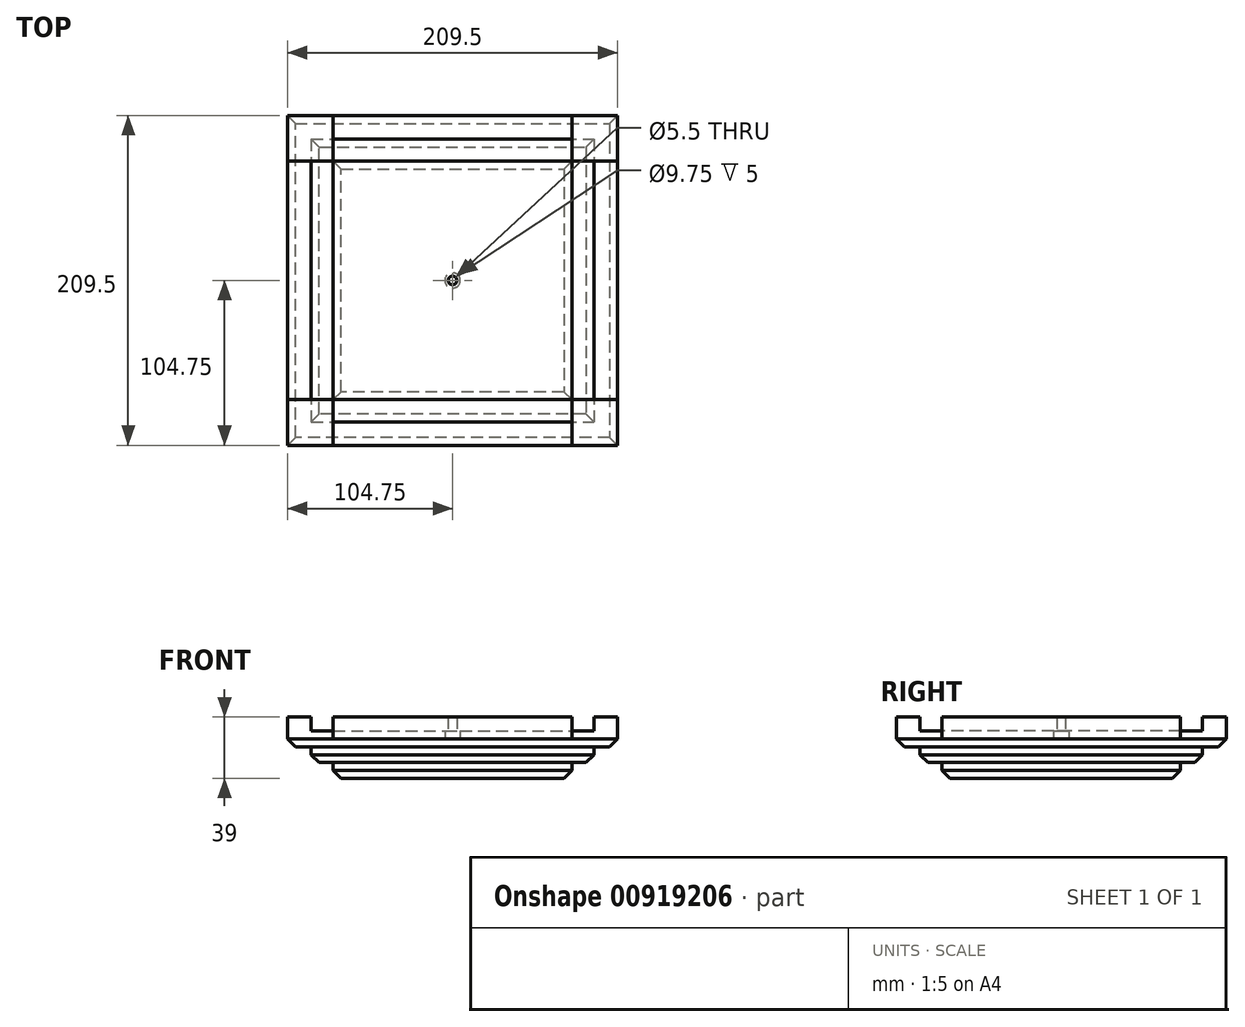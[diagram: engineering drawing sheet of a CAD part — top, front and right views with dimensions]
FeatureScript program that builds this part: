
annotation { "Feature Type Name" : "Feature", "Feature Type Description" : "" }
export const myFeature = defineFeature(function(context is Context, id is Id, definition is map)
    precondition{}
    {
        {
            var Q0;
            Q0=qCreatedBy(makeId("Top.planeOp"),FACE);
            var sketch = newSketch(context, id + "F0", { "sketchPlane" : qUnion([Q0])});
            skLineSegment(sketch, "E0.bottom", {"start": v(-104.75, 104.75) * mm, "end": v(104.75, 104.75) * mm});
            skLineSegment(sketch, "E0.top", {"start": v(-104.75, -104.75) * mm, "end": v(104.75, -104.75) * mm});
            skLineSegment(sketch, "E0.left", {"start": v(-104.75, 104.75) * mm, "end": v(-104.75, -104.75) * mm});
            skLineSegment(sketch, "E0.right", {"start": v(104.75, 104.75) * mm, "end": v(104.75, -104.75) * mm});
            skLineSegment(sketch, "E1.bottom", {"start": v(-75.75, 75.75) * mm, "end": v(75.75, 75.75) * mm});
            skLineSegment(sketch, "E1.top", {"start": v(-75.75, -75.75) * mm, "end": v(75.75, -75.75) * mm});
            skLineSegment(sketch, "E1.left", {"start": v(-75.75, 75.75) * mm, "end": v(-75.75, -75.75) * mm});
            skLineSegment(sketch, "E1.right", {"start": v(75.75, 75.75) * mm, "end": v(75.75, -75.75) * mm});
            skLineSegment(sketch, "E2.0", {"start": v(-89.75, 89.75) * mm, "end": v(-89.75, -89.75) * mm});
            skLineSegment(sketch, "E2.1", {"start": v(-89.75, 89.75) * mm, "end": v(89.75, 89.75) * mm});
            skLineSegment(sketch, "E2.2", {"start": v(89.75, 89.75) * mm, "end": v(89.75, -89.75) * mm});
            skLineSegment(sketch, "E2.3", {"start": v(-89.75, -89.75) * mm, "end": v(89.75, -89.75) * mm});
            skLineSegment(sketch, "E3.bottom", {"start": v(-75.75, 75.75) * mm, "end": v(-104.75, 75.75) * mm});
            skLineSegment(sketch, "E3.top", {"start": v(-75.75, 104.75) * mm, "end": v(-104.75, 104.75) * mm});
            skLineSegment(sketch, "E3.left", {"start": v(-75.75, 75.75) * mm, "end": v(-75.75, 104.75) * mm});
            skLineSegment(sketch, "E3.right", {"start": v(-104.75, 75.75) * mm, "end": v(-104.75, 104.75) * mm});
            skLineSegment(sketch, "E4.bottom", {"start": v(75.75, 75.75) * mm, "end": v(104.75, 75.75) * mm});
            skLineSegment(sketch, "E4.top", {"start": v(75.75, 104.75) * mm, "end": v(104.75, 104.75) * mm});
            skLineSegment(sketch, "E4.left", {"start": v(75.75, 75.75) * mm, "end": v(75.75, 104.75) * mm});
            skLineSegment(sketch, "E4.right", {"start": v(104.75, 75.75) * mm, "end": v(104.75, 104.75) * mm});
            skLineSegment(sketch, "E5.bottom", {"start": v(75.75, -75.75) * mm, "end": v(104.75, -75.75) * mm});
            skLineSegment(sketch, "E5.top", {"start": v(75.75, -104.75) * mm, "end": v(104.75, -104.75) * mm});
            skLineSegment(sketch, "E5.left", {"start": v(75.75, -75.75) * mm, "end": v(75.75, -104.75) * mm});
            skLineSegment(sketch, "E5.right", {"start": v(104.75, -75.75) * mm, "end": v(104.75, -104.75) * mm});
            skLineSegment(sketch, "E6.bottom", {"start": v(-75.75, -75.75) * mm, "end": v(-104.75, -75.75) * mm});
            skLineSegment(sketch, "E6.top", {"start": v(-75.75, -104.75) * mm, "end": v(-104.75, -104.75) * mm});
            skLineSegment(sketch, "E6.left", {"start": v(-75.75, -75.75) * mm, "end": v(-75.75, -104.75) * mm});
            skLineSegment(sketch, "E6.right", {"start": v(-104.75, -75.75) * mm, "end": v(-104.75, -104.75) * mm});
            skLineSegment(sketch, "E7.left", {"start": v(-89.75, -89.75) * mm, "end": v(-89.75, 89.75) * mm});
            skLineSegment(sketch, "E7.right", {"start": v(89.75, -89.75) * mm, "end": v(89.75, 89.75) * mm});
            skPoint(sketch, "E8", {"position": v(0, 0) * mm});
            skSolve(sketch);
        }
        {
            var Q0;
            Q0=makeQuery(id+"F0.imprint","IMPRINT",FACE,{"disambiguationData":[TD([[makeQuery(id+"F0.imprint","IMPRINT",EDGE,{"derivedFrom":sQuery(id+"F0.wireOp",EDGE,"E1.bottom")}),-1.0]])]});
            extrude(context, id + "F1", {"entities" : qUnion([Q0]), "depth" : 14 * mm, "offsetDistance" : 25 * mm});
        }
        {
            var Q0;
            {var subQ0=sQuery(id+"F0.wireOp",EDGE,"E1.bottom");Q0=makeQuery(id+"F0.imprint","IMPRINT",FACE,{"disambiguationData":[TD([[makeQuery(id+"F0.imprint","IMPRINT",EDGE,{"derivedFrom":subQ0}),1.0]])]});}
            var Q1;
            {var subQ0=sQuery(id+"F0.wireOp",EDGE,"E1.left");Q1=makeQuery(id+"F0.imprint","IMPRINT",FACE,{"disambiguationData":[TD([[makeQuery(id+"F0.imprint","IMPRINT",EDGE,{"derivedFrom":subQ0}),-1.0]])]});}
            var Q2;
            {var subQ0=sQuery(id+"F0.wireOp",EDGE,"E1.right");Q2=makeQuery(id+"F0.imprint","IMPRINT",FACE,{"disambiguationData":[TD([[makeQuery(id+"F0.imprint","IMPRINT",EDGE,{"derivedFrom":subQ0}),1.0]])]});}
            var Q3;
            {var subQ0=sQuery(id+"F0.wireOp",EDGE,"E1.top");Q3=makeQuery(id+"F0.imprint","IMPRINT",FACE,{"disambiguationData":[TD([[makeQuery(id+"F0.imprint","IMPRINT",EDGE,{"derivedFrom":subQ0}),-1.0]])]});}
            extrude(context, id + "F2", {"entities" : qUnion([Q0, Q1, Q2, Q3]), "operationType" : NewBodyOperationType.ADD, "depth" : 5 * mm, "offsetDistance" : 25 * mm});
        }
        {
            var Q0;
            {var subQ0=sQuery(id+"F0.wireOp",EDGE,"E3.bottom");var subQ1=sQuery(id+"F0.wireOp",EDGE,"E0.left");var subQ2=makeQuery(id+"F0.imprint","INTERSECT",VERTEX,{"derivedFrom":[subQ1,subQ0]});Q0=makeQuery(id+"F0.imprint","IMPRINT",FACE,{"disambiguationData":[TD([[makeQuery(id+"F0.imprint","IMPRINT",EDGE,{"disambiguationData":[TD([[subQ2,-1.0]])],"derivedFrom":subQ1}),1.0]])]});}
            var Q1;
            {var subQ0=sQuery(id+"F0.wireOp",EDGE,"E3.left");var subQ1=sQuery(id+"F0.wireOp",EDGE,"E0.bottom");var subQ2=makeQuery(id+"F0.imprint","INTERSECT",VERTEX,{"derivedFrom":[subQ1,subQ0]});Q1=makeQuery(id+"F0.imprint","IMPRINT",FACE,{"disambiguationData":[TD([[makeQuery(id+"F0.imprint","IMPRINT",EDGE,{"disambiguationData":[TD([[subQ2,-1.0]])],"derivedFrom":subQ1}),-1.0]])]});}
            var Q2;
            {var subQ0=sQuery(id+"F0.wireOp",EDGE,"E4.bottom");var subQ1=sQuery(id+"F0.wireOp",EDGE,"E0.right");var subQ2=makeQuery(id+"F0.imprint","INTERSECT",VERTEX,{"derivedFrom":[subQ1,subQ0]});Q2=makeQuery(id+"F0.imprint","IMPRINT",FACE,{"disambiguationData":[TD([[makeQuery(id+"F0.imprint","IMPRINT",EDGE,{"disambiguationData":[TD([[subQ2,-1.0]])],"derivedFrom":subQ1}),-1.0]])]});}
            var Q3;
            {var subQ0=sQuery(id+"F0.wireOp",EDGE,"E6.left");var subQ1=sQuery(id+"F0.wireOp",EDGE,"E0.top");var subQ2=makeQuery(id+"F0.imprint","INTERSECT",VERTEX,{"derivedFrom":[subQ1,subQ0]});Q3=makeQuery(id+"F0.imprint","IMPRINT",FACE,{"disambiguationData":[TD([[makeQuery(id+"F0.imprint","IMPRINT",EDGE,{"disambiguationData":[TD([[subQ2,-1.0]])],"derivedFrom":subQ1}),1.0]])]});}
            extrude(context, id + "F3", {"entities" : qUnion([Q0, Q1, Q2, Q3]), "operationType" : NewBodyOperationType.ADD, "depth" : 14 * mm, "offsetDistance" : 25 * mm});
        }
        {
            var Q0;
            {var subQ0=sQuery(id+"F0.wireOp",EDGE,"E5.bottom");var subQ1=sQuery(id+"F0.wireOp",EDGE,"E4.bottom");var subQ2=sQuery(id+"F0.wireOp",EDGE,"E2.2");var subQ3=sQuery(id+"F0.wireOp",EDGE,"E6.bottom");var subQ4=sQuery(id+"F0.wireOp",EDGE,"E3.bottom");var subQ5=sQuery(id+"F0.wireOp",EDGE,"E2.0");var subQ6=sQuery(id+"F0.wireOp",EDGE,"E6.left");var subQ7=sQuery(id+"F0.wireOp",EDGE,"E5.left");var subQ8=sQuery(id+"F0.wireOp",EDGE,"E2.3");var subQ9=sQuery(id+"F0.wireOp",EDGE,"E4.left");var subQ10=sQuery(id+"F0.wireOp",EDGE,"E3.left");var subQ11=sQuery(id+"F0.wireOp",EDGE,"E2.1");var subQ12=sQuery(id+"F0.wireOp",EDGE,"E1.right");var subQ13=sQuery(id+"F0.wireOp",EDGE,"E1.left");var subQ14=sQuery(id+"F0.wireOp",EDGE,"E1.top");var subQ15=sQuery(id+"F0.wireOp",EDGE,"E1.bottom");Q0=makeQuery(id+"F3.boolean.opBoolean","MERGE",FACE,{"derivedFrom":[makeQuery(id+"F2.boolean.opBoolean","MERGE",FACE,{"derivedFrom":[makeQuery(id+"F1.opExtrude","CAP_FACE",FACE,{"disambiguationData":[OSD([subQ15,subQ14,subQ13,subQ12])],"isStart":true}),makeQuery(id+"F2.opExtrude","CAP_FACE",FACE,{"disambiguationData":[OSD([subQ15,subQ11,subQ10,subQ9])],"isStart":true}),makeQuery(id+"F2.opExtrude","CAP_FACE",FACE,{"disambiguationData":[OSD([subQ14,subQ8,subQ7,subQ6])],"isStart":true}),makeQuery(id+"F2.opExtrude","CAP_FACE",FACE,{"disambiguationData":[OSD([subQ13,subQ5,subQ4,subQ3])],"isStart":true}),makeQuery(id+"F2.opExtrude","CAP_FACE",FACE,{"disambiguationData":[OSD([subQ12,subQ2,subQ1,subQ0])],"isStart":true})]}),makeQuery(id+"F3.opExtrude","CAP_FACE",FACE,{"disambiguationData":[OSD([sQuery(id+"F0.wireOp",EDGE,"E0.bottom"),subQ11,subQ10,subQ9])],"isStart":true}),makeQuery(id+"F3.opExtrude","CAP_FACE",FACE,{"disambiguationData":[OSD([sQuery(id+"F0.wireOp",EDGE,"E0.top"),subQ8,subQ7,subQ6])],"isStart":true}),makeQuery(id+"F3.opExtrude","CAP_FACE",FACE,{"disambiguationData":[OSD([sQuery(id+"F0.wireOp",EDGE,"E0.left"),subQ5,subQ4,subQ3])],"isStart":true}),makeQuery(id+"F3.opExtrude","CAP_FACE",FACE,{"disambiguationData":[OSD([sQuery(id+"F0.wireOp",EDGE,"E0.right"),subQ2,subQ1,subQ0])],"isStart":true})]});}
            var sketch = newSketch(context, id + "F4", { "sketchPlane" : qUnion([Q0])});
            skCircle(sketch, "E9.cCircle", {"center": v(0, 0) * mm, "radius": 132.62 * mm, "construction": true});
            skLineSegment(sketch, "E9.0", {"start": v(-95.02, -133.58) * mm, "end": v(-156.4, 49.1) * mm});
            skLineSegment(sketch, "E9.1", {"start": v(-156.4, 49.1) * mm, "end": v(-1.65, 163.92) * mm});
            skLineSegment(sketch, "E9.2", {"start": v(-1.65, 163.92) * mm, "end": v(155.4, 52.22) * mm});
            skLineSegment(sketch, "E9.3", {"start": v(155.4, 52.22) * mm, "end": v(97.68, -131.65) * mm});
            skLineSegment(sketch, "E9.4", {"start": v(97.68, -131.65) * mm, "end": v(-95.02, -133.58) * mm});
            skPoint(sketch, "E9.0.midPoint", {"position": v(-125.71, -42.25) * mm});
            skLineSegment(sketch, "E10.0", {"start": v(162.35, 22.73) * mm, "end": v(71.78, -147.38) * mm});
            skLineSegment(sketch, "E10.1", {"start": v(71.78, -147.38) * mm, "end": v(-117.98, -113.81) * mm});
            skLineSegment(sketch, "E10.2", {"start": v(-117.98, -113.81) * mm, "end": v(-144.7, 77.04) * mm});
            skLineSegment(sketch, "E10.3", {"start": v(-144.7, 77.04) * mm, "end": v(28.56, 161.43) * mm});
            skLineSegment(sketch, "E10.4", {"start": v(28.56, 161.43) * mm, "end": v(162.35, 22.73) * mm});
            skPoint(sketch, "E10.0.midPoint", {"position": v(117.07, -62.33) * mm});
            skLineSegment(sketch, "E11.0", {"start": v(157.89, -44.1) * mm, "end": v(6.85, -163.79) * mm});
            skLineSegment(sketch, "E11.1", {"start": v(6.85, -163.79) * mm, "end": v(-153.65, -57.13) * mm});
            skLineSegment(sketch, "E11.2", {"start": v(-153.65, -57.13) * mm, "end": v(-101.82, 128.48) * mm});
            skLineSegment(sketch, "E11.3", {"start": v(-101.82, 128.48) * mm, "end": v(90.73, 136.54) * mm});
            skLineSegment(sketch, "E11.4", {"start": v(90.73, 136.54) * mm, "end": v(157.89, -44.1) * mm});
            skPoint(sketch, "E11.0.midPoint", {"position": v(82.37, -103.94) * mm});
            skLineSegment(sketch, "E12.0", {"start": v(-30.47, -161.08) * mm, "end": v(-162.6, -20.8) * mm});
            skLineSegment(sketch, "E12.1", {"start": v(-162.6, -20.8) * mm, "end": v(-70.03, 148.22) * mm});
            skLineSegment(sketch, "E12.2", {"start": v(-70.03, 148.22) * mm, "end": v(119.33, 112.4) * mm});
            skLineSegment(sketch, "E12.3", {"start": v(119.33, 112.4) * mm, "end": v(143.78, -78.75) * mm});
            skLineSegment(sketch, "E12.4", {"start": v(143.78, -78.75) * mm, "end": v(-30.47, -161.08) * mm});
            skPoint(sketch, "E12.0.midPoint", {"position": v(-96.54, -90.94) * mm});
            skLineSegment(sketch, "E13", {"start": v(0, 76.18) * mm, "end": v(0, -35.98) * mm, "construction": true});
            skLineSegment(sketch, "E14", {"start": v(-66.42, 0) * mm, "end": v(50.94, 0) * mm, "construction": true});
            skSolve(sketch);
        }
        {
            var Q0;
            {var subQ0=sQuery(id+"F0.wireOp",EDGE,"E3.left");var subQ1=sQuery(id+"F0.wireOp",EDGE,"E0.bottom");var subQ2=makeQuery(id+"F0.imprint","INTERSECT",VERTEX,{"derivedFrom":[subQ1,subQ0]});Q0=makeQuery(id+"F0.imprint","IMPRINT",FACE,{"disambiguationData":[TD([[makeQuery(id+"F0.imprint","IMPRINT",EDGE,{"disambiguationData":[TD([[subQ2,-1.0]])],"derivedFrom":subQ1}),-1.0]])]});}
            var Q1;
            {var subQ0=sQuery(id+"F0.wireOp",EDGE,"E3.left");var subQ9=sQuery(id+"F0.wireOp",EDGE,"E0.bottom");var subQ11=makeQuery(id+"F0.imprint","INTERSECT",VERTEX,{"derivedFrom":[subQ9,subQ0]});Q1=makeQuery(id+"F0.imprint","IMPRINT",FACE,{"disambiguationData":[TD([[makeQuery(id+"F0.imprint","IMPRINT",EDGE,{"disambiguationData":[TD([[subQ11,1.0]])],"derivedFrom":subQ9}),-1.0]])]});}
            var Q2;
            {var subQ0=sQuery(id+"F0.wireOp",EDGE,"E3.bottom");var subQ1=sQuery(id+"F0.wireOp",EDGE,"E0.left");var subQ2=makeQuery(id+"F0.imprint","INTERSECT",VERTEX,{"derivedFrom":[subQ1,subQ0]});Q2=makeQuery(id+"F0.imprint","IMPRINT",FACE,{"disambiguationData":[TD([[makeQuery(id+"F0.imprint","IMPRINT",EDGE,{"disambiguationData":[TD([[subQ2,-1.0]])],"derivedFrom":subQ1}),1.0]])]});}
            var Q3;
            {var subQ0=sQuery(id+"F0.wireOp",EDGE,"E6.left");var subQ5=sQuery(id+"F0.wireOp",EDGE,"E0.top");var subQ6=makeQuery(id+"F0.imprint","INTERSECT",VERTEX,{"derivedFrom":[subQ5,subQ0]});Q3=makeQuery(id+"F0.imprint","IMPRINT",FACE,{"disambiguationData":[TD([[makeQuery(id+"F0.imprint","IMPRINT",EDGE,{"disambiguationData":[TD([[subQ6,1.0]])],"derivedFrom":subQ5}),1.0]])]});}
            var Q4;
            {var subQ0=sQuery(id+"F0.wireOp",EDGE,"E6.left");var subQ1=sQuery(id+"F0.wireOp",EDGE,"E0.top");var subQ2=makeQuery(id+"F0.imprint","INTERSECT",VERTEX,{"derivedFrom":[subQ1,subQ0]});Q4=makeQuery(id+"F0.imprint","IMPRINT",FACE,{"disambiguationData":[TD([[makeQuery(id+"F0.imprint","IMPRINT",EDGE,{"disambiguationData":[TD([[subQ2,-1.0]])],"derivedFrom":subQ1}),1.0]])]});}
            var Q5;
            {var subQ5=sQuery(id+"F0.wireOp",EDGE,"E0.right");var subQ6=sQuery(id+"F0.wireOp",EDGE,"E0.top");var subQ7=makeQuery(id+"F0.imprint","INTERSECT",VERTEX,{"derivedFrom":[subQ6,subQ5]});Q5=makeQuery(id+"F0.imprint","IMPRINT",FACE,{"disambiguationData":[TD([[makeQuery(id+"F0.imprint","IMPRINT",EDGE,{"disambiguationData":[TD([[subQ7,1.0]])],"derivedFrom":subQ6}),1.0]])]});}
            var Q6;
            {var subQ0=sQuery(id+"F0.wireOp",EDGE,"E4.bottom");var subQ1=sQuery(id+"F0.wireOp",EDGE,"E0.right");var subQ2=makeQuery(id+"F0.imprint","INTERSECT",VERTEX,{"derivedFrom":[subQ1,subQ0]});Q6=makeQuery(id+"F0.imprint","IMPRINT",FACE,{"disambiguationData":[TD([[makeQuery(id+"F0.imprint","IMPRINT",EDGE,{"disambiguationData":[TD([[subQ2,-1.0]])],"derivedFrom":subQ1}),-1.0]])]});}
            var Q7;
            {var subQ5=sQuery(id+"F0.wireOp",EDGE,"E0.right");var subQ6=sQuery(id+"F0.wireOp",EDGE,"E0.bottom");var subQ7=makeQuery(id+"F0.imprint","INTERSECT",VERTEX,{"derivedFrom":[subQ6,subQ5]});Q7=makeQuery(id+"F0.imprint","IMPRINT",FACE,{"disambiguationData":[TD([[makeQuery(id+"F0.imprint","IMPRINT",EDGE,{"disambiguationData":[TD([[subQ7,1.0]])],"derivedFrom":subQ6}),-1.0]])]});}
            extrude(context, id + "F5", {"entities" : qUnion([Q0, Q1, Q2, Q3, Q4, Q5, Q6, Q7]), "operationType" : NewBodyOperationType.ADD, "oppositeDirection" : true, "depth" : 5 * mm, "offsetDistance" : 25 * mm});
        }
        {
            var Q0;
            {var subQ0=sQuery(id+"F0.wireOp",EDGE,"E1.bottom");Q0=makeQuery(id+"F0.imprint","IMPRINT",FACE,{"disambiguationData":[TD([[makeQuery(id+"F0.imprint","IMPRINT",EDGE,{"derivedFrom":subQ0}),1.0]])]});}
            var Q1;
            {var subQ0=sQuery(id+"F0.wireOp",EDGE,"E1.left");Q1=makeQuery(id+"F0.imprint","IMPRINT",FACE,{"disambiguationData":[TD([[makeQuery(id+"F0.imprint","IMPRINT",EDGE,{"derivedFrom":subQ0}),-1.0]])]});}
            var Q2;
            {var subQ0=sQuery(id+"F0.wireOp",EDGE,"E1.top");Q2=makeQuery(id+"F0.imprint","IMPRINT",FACE,{"disambiguationData":[TD([[makeQuery(id+"F0.imprint","IMPRINT",EDGE,{"derivedFrom":subQ0}),-1.0]])]});}
            var Q3;
            {var subQ0=sQuery(id+"F0.wireOp",EDGE,"E1.right");Q3=makeQuery(id+"F0.imprint","IMPRINT",FACE,{"disambiguationData":[TD([[makeQuery(id+"F0.imprint","IMPRINT",EDGE,{"derivedFrom":subQ0}),1.0]])]});}
            var Q4;
            {var subQ0=sQuery(id+"F0.wireOp",EDGE,"E2.3");var subQ1=sQuery(id+"F0.wireOp",EDGE,"E2.2");var subQ2=makeQuery(id+"F0.imprint","INTERSECT",VERTEX,{"derivedFrom":[subQ1,subQ0]});Q4=makeQuery(id+"F0.imprint","IMPRINT",FACE,{"disambiguationData":[TD([[makeQuery(id+"F0.imprint","IMPRINT",EDGE,{"disambiguationData":[TD([[subQ2,1.0]])],"derivedFrom":subQ1}),-1.0]])]});}
            var Q5;
            {var subQ0=sQuery(id+"F0.wireOp",EDGE,"E2.2");var subQ1=sQuery(id+"F0.wireOp",EDGE,"E2.1");var subQ2=makeQuery(id+"F0.imprint","INTERSECT",VERTEX,{"derivedFrom":[subQ1,subQ0]});Q5=makeQuery(id+"F0.imprint","IMPRINT",FACE,{"disambiguationData":[TD([[makeQuery(id+"F0.imprint","IMPRINT",EDGE,{"disambiguationData":[TD([[subQ2,1.0]])],"derivedFrom":subQ1}),-1.0]])]});}
            var Q6;
            {var subQ0=sQuery(id+"F0.wireOp",EDGE,"E3.bottom");var subQ1=sQuery(id+"F0.wireOp",EDGE,"E2.0");var subQ2=makeQuery(id+"F0.imprint","INTERSECT",VERTEX,{"derivedFrom":[subQ1,subQ0]});Q6=makeQuery(id+"F0.imprint","IMPRINT",FACE,{"disambiguationData":[TD([[makeQuery(id+"F0.imprint","IMPRINT",EDGE,{"disambiguationData":[TD([[subQ2,1.0]])],"derivedFrom":subQ1}),1.0]])]});}
            var Q7;
            Q7=makeQuery(id+"F0.imprint","IMPRINT",FACE,{"disambiguationData":[TD([[makeQuery(id+"F0.imprint","IMPRINT",EDGE,{"derivedFrom":sQuery(id+"F0.wireOp",EDGE,"E1.bottom")}),-1.0]])]});
            var Q8;
            {var subQ0=sQuery(id+"F0.wireOp",EDGE,"E6.bottom");var subQ1=sQuery(id+"F0.wireOp",EDGE,"E2.0");var subQ2=makeQuery(id+"F0.imprint","INTERSECT",VERTEX,{"derivedFrom":[subQ1,subQ0]});Q8=makeQuery(id+"F0.imprint","IMPRINT",FACE,{"disambiguationData":[TD([[makeQuery(id+"F0.imprint","IMPRINT",EDGE,{"disambiguationData":[TD([[subQ2,-1.0]])],"derivedFrom":subQ1}),1.0]])]});}
            var Q9;
            Q9=sQuery(id+"F0.wireOp",EDGE,"E2.3");
            var Q10;
            Q10=sQuery(id+"F0.wireOp",EDGE,"E2.0");
            var Q11;
            Q11=sQuery(id+"F0.wireOp",EDGE,"E2.2");
            var Q12;
            Q12=sQuery(id+"F0.wireOp",EDGE,"E2.1");
            extrude(context, id + "F6", {"entities" : qUnion([Q0, Q1, Q2, Q3, Q4, Q5, Q6, Q7, Q8]), "operationType" : NewBodyOperationType.ADD, "surfaceEntities" : qUnion([Q9, Q10, Q11, Q12]), "oppositeDirection" : true, "depth" : 15 * mm, "offsetDistance" : 25 * mm});
        }
        {
            var Q0;
            Q0=makeQuery(id+"F0.imprint","IMPRINT",FACE,{"disambiguationData":[TD([[makeQuery(id+"F0.imprint","IMPRINT",EDGE,{"derivedFrom":sQuery(id+"F0.wireOp",EDGE,"E1.bottom")}),-1.0]])]});
            extrude(context, id + "F7", {"entities" : qUnion([Q0]), "operationType" : NewBodyOperationType.ADD, "oppositeDirection" : true, "depth" : 25 * mm, "offsetDistance" : 25 * mm});
        }
        {
            var Q0;
            Q0=makeQuery(id+"F7.opExtrude","CAP_EDGE",EDGE,{"disambiguationData":[OSD([sQuery(id+"F0.wireOp",EDGE,"E1.bottom")])],"isStart":false});
            var Q1;
            Q1=makeQuery(id+"F6.opExtrude","CAP_EDGE",EDGE,{"disambiguationData":[OSD([sQuery(id+"F0.wireOp",EDGE,"E2.1")])],"isStart":false});
            var Q2;
            Q2=makeQuery(id+"F5.opExtrude","CAP_EDGE",EDGE,{"disambiguationData":[OSD([sQuery(id+"F0.wireOp",EDGE,"E0.bottom")])],"isStart":false});
            var Q3;
            Q3=makeQuery(id+"F5.opExtrude","CAP_EDGE",EDGE,{"disambiguationData":[OSD([sQuery(id+"F0.wireOp",EDGE,"E0.right")])],"isStart":false});
            var Q4;
            Q4=makeQuery(id+"F6.opExtrude","CAP_EDGE",EDGE,{"disambiguationData":[OSD([sQuery(id+"F0.wireOp",EDGE,"E2.2")])],"isStart":false});
            var Q5;
            Q5=makeQuery(id+"F7.opExtrude","CAP_EDGE",EDGE,{"disambiguationData":[OSD([sQuery(id+"F0.wireOp",EDGE,"E1.right")])],"isStart":false});
            var Q6;
            Q6=makeQuery(id+"F7.opExtrude","CAP_EDGE",EDGE,{"disambiguationData":[OSD([sQuery(id+"F0.wireOp",EDGE,"E1.top")])],"isStart":false});
            var Q7;
            Q7=makeQuery(id+"F6.opExtrude","CAP_EDGE",EDGE,{"disambiguationData":[OSD([sQuery(id+"F0.wireOp",EDGE,"E2.3")])],"isStart":false});
            var Q8;
            Q8=makeQuery(id+"F5.opExtrude","CAP_EDGE",EDGE,{"disambiguationData":[OSD([sQuery(id+"F0.wireOp",EDGE,"E0.top")])],"isStart":false});
            var Q9;
            Q9=makeQuery(id+"F5.opExtrude","CAP_EDGE",EDGE,{"disambiguationData":[OSD([sQuery(id+"F0.wireOp",EDGE,"E0.left")])],"isStart":false});
            var Q10;
            Q10=makeQuery(id+"F6.opExtrude","CAP_EDGE",EDGE,{"disambiguationData":[OSD([sQuery(id+"F0.wireOp",EDGE,"E2.0")])],"isStart":false});
            var Q11;
            Q11=makeQuery(id+"F7.opExtrude","CAP_EDGE",EDGE,{"disambiguationData":[OSD([sQuery(id+"F0.wireOp",EDGE,"E1.left")])],"isStart":false});
            chamfer(context, id + "F8", {"entities" : qUnion([Q0, Q1, Q2, Q3, Q4, Q5, Q6, Q7, Q8, Q9, Q10, Q11]), "width" : 5 * mm, "tangentPropagation" : true});
        }
        {
            var Q0;
            Q0=sQuery(id+"F4.wireOp",VERTEX,"E9.cCircle.center");
            var Q1;
            Q1=makeQuery(id+"F1.opExtrude","SWEPT_BODY",BODY,{"disambiguationData":[OSD([sQuery(id+"F0.wireOp",EDGE,"E1.bottom"),sQuery(id+"F0.wireOp",EDGE,"E1.top"),sQuery(id+"F0.wireOp",EDGE,"E1.left"),sQuery(id+"F0.wireOp",EDGE,"E1.right")])]});
            hole(context, id + "F9", {"style" : HoleStyle.C_BORE, "endStyle" : HoleEndStyle.THROUGH, "standardTappedOrClearance" : lookupTablePath({ "fit" : "Normal", "standard" : "ISO", "size" : "M5", "type" : "Clearance" }), "standardBlindInLast" : lookupTablePath({ "fit" : "Normal", "standard" : "ISO", "size" : "M5", "type" : "Clearance" }), "holeDiameter" : 5.5 * mm, "cBoreDiameter" : 9.75 * mm, "cBoreDepth" : 5 * mm, "majorDiameter" : 5 * mm, "isTappedThrough" : true, "tappedDepth" : 12 * mm, "tapClearance" : 3, "locations" : qUnion([Q0]), "scope" : qUnion([Q1])});
        }
    });
